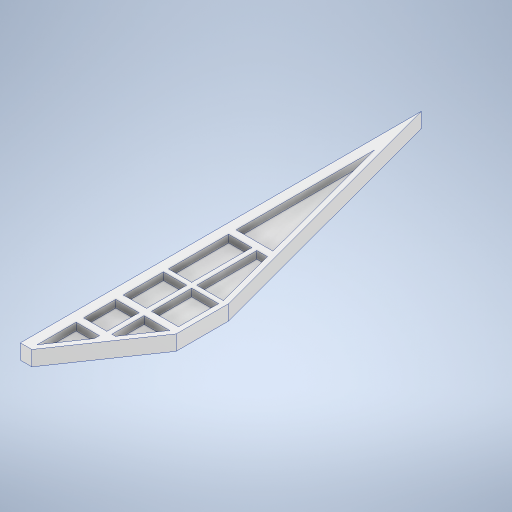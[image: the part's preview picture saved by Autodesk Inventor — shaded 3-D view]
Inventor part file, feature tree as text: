
AUTODESK INVENTOR PART (.ipt)
format: ipt  version: 2024 (Build 280153000, 153)  size: 320,512 bytes
history: native  units: mm
features: extrude x2, sketch x2, projected_geometry x1
ambient origin geometry x8: Origin, YZ Plane, XZ Plane, XY Plane, X Axis, Y Axis, Z Axis, Center Point
bodies: Solid1 (feature_tree)
feature tree (5):
  extrude  "Extrusion1"  Depth=200.0mm
  extrude  "Extrusion2"  Depth=20.0mm
  sketch  "Sketch1"  dims[d0=600.0mm d1=200.0mm]
  sketch  "Sketch2"  dims[d2=160.0mm d3=20.0mm d4=30.0mm d5=0.0mm d6=10.0mm d7=15.0mm d8=15.0mm d9=120.0mm d10=80.0mm d11=10.0mm d12=15.0mm d13=0.0mm d15=15.0mm d16=10.0mm d17=20.0mm]
  projected_geometry  "Projected Loop1"
